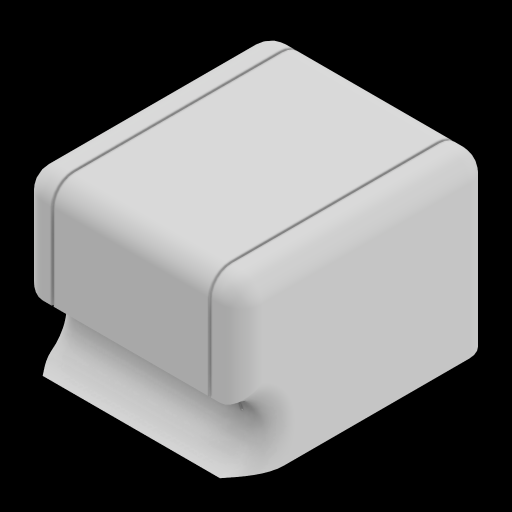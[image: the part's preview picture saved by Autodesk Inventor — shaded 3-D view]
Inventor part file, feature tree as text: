
AUTODESK INVENTOR PART (.ipt)
format: ipt  version: 2024 (Build 280153000, 153)  size: 277,504 bytes
history: native  units: in
note: dims shown in document units (in); Inventor stores cm internally (conversion verified against a paired STEP export)
features: sketch x6, extrude x6, projected_geometry x2, other x1, plane x1, mirror x1, fillet x1
ambient origin geometry x8: Origin, YZ Plane, XZ Plane, XY Plane, X Axis, Y Axis, Z Axis, Center Point
bodies: Solid1 (feature_tree)
feature tree (18):
  sketch  "Sketch1"  dims[d0=0.387in d1=0.763in d2=0.0in]
  extrude  "CAP"  Depth=0.763in TaperAngle=0.0deg
  sketch  "Sketch2"  dims[d7=0.92in d12=0.92in]
  other  "SHEATHING"
  extrude  "WIRE APROX"  Depth=0.92in
  plane  "Work Plane1"
  extrude  "RAXOR1 EXT"  Depth=0.0785in
  sketch  "Sketch11"  dims[d20=0.02in d21=3.0in d22=0.0in]
  sketch  "Sketch12"  dims[d25=0.129in d26=1.5in d29=0.77in d30=0.012in d31=0.0in d32=0.5504in d35=0.46in d46=1.3in d47=0.0in d48=1.3in d49=0.0in d54=0.012in d55=0.0in d82=0.6865in d83=90.0deg d84=0.6184in d85=1.0165in d86=0.77in d87=1.5in d88=1.4776in d89=0.6308in d90=0.823in d95=0.125in d23=0.5in d24=0.0344in d33=0.0344in d36=0.0344in d37=0.5in d38=0.0344in d50=0.5in d51=0.0344in d52=0.5in d53=0.0344in d56=0.5in d57=0.0344in d58=0.5in d59=0.0344in d63=0.5in d64=0.0344in d65=0.5in d66=0.0344in d67=0.0344in d74=0.5in d75=0.0344in d76=0.5in d77=0.0344in d96=0.0in d97=0.0in d98=0.0in]
  extrude  "WORKPIECE"  TaperAngle=360.0deg  [1 undecoded]
  extrude  "CAP CUTOUT"  Depth=3.0in TaperAngle=0.0deg
  extrude  "RAZ CUTOUT1"  Depth=0.125in
  mirror  "Mirror1"
  fillet  "Fillet8"  Radius=0.77in
  sketch  "Sketch3"  dims[d15=0.0785in d16=0.0785in]
  sketch  "Sketch5"  dims[d18=0.3815in d19=360.0deg]
  projected_geometry  "Projected Loop6"
  projected_geometry  "Projected Loop7"
note: 1 required parameter value undecoded (feature->parameter linkage not recoverable at this tier; creation-order binding heuristic only, values carry confidence <= 0.55)
